# Revit family: Capsule V 2100-12500
name_source: partatom
category: Оборудование
units: mm (PartAtom-declared; Revit-internal decimal feet)

## family parameters
Всегда вертикально = Да
Классификация = Нет
На основе рабочей плоскости = Нет
Общий = Нет
При загрузке вырезать с полостями = Нет
Размер круглого соединителя = Использовать диаметр
Тип детали = Нормальный
Точка расчета площади = Нет

## types (10) — shared parameters
ADSK_Единица измерения = шт.
ADSK_Завод-изготовитель = ООО «Турков»
ADSK_Количество = 1
ADSK_Наименование = Вытяжная установка
КА длина = 180 мм
КА ширина = 82 мм
Крепеж Y = 23 мм
Толщина крышки = 50 мм
высота КА = 52 мм

## per-type parameters (varying)
| type | A ширина | ADSK_Количество фаз | ADSK_Масса | ADSK_Напряжение | ADSK_Номинальная мощность | ADSK_Расход воздуха приточный | ADSK_Свободный напор воздуха | ADSK_Ток | B высота | ВВ длина | ВВ толщина | ВВ ширина | Крепеж X | С глубина | СЗ_фильтры |
| VBox 6100 | 635 мм | 1 | 75 | 220 В | 330 Вт | 600.0 м³/ч | 189.0 Па | 1 А | 900 мм | 800 мм | 180 мм | 500 мм | 52 мм | 650 мм | 350 мм |
| VBox 4100 | 635 мм | 1 | 100 | 220 В | 840 Вт | 4000.0 м³/ч | 253.0 Па | 2 А | 850 мм | 700 мм | 190 мм | 400 мм | 7 мм | 550 мм | 400 мм |
| VBox 2100 | 528 мм | 1 | 75 | 220 В | 330 Вт | 2100.0 м³/ч | 189.0 Па | 1 А | 656 мм | 500 мм | 180 мм | 250 мм | 52 мм | 437 мм | 350 мм |
| VBox 3100 | 635 мм | 1 | 80 | 220 В | 750 Вт | 3000.0 м³/ч | 291.0 Па | 5 А | 750 мм | 600 мм | 190 мм | 300 мм | 52 мм | 450 мм | 300 мм |
| VBox 5100 | 635 мм | 3 | 105 | 380 В | 2500 Вт | 5000.0 м³/ч | 620.0 Па | 4 А | 850 мм | 700 мм | 190 мм | 400 мм | 7 мм | 550 мм | 400 мм |
| VBox 7100 | 635 мм | 3 | 120 | 380 В | 0 Вт | 6000.0 м³/ч | 291.0 Па | 0 А | 900 мм | 800 мм | 190 мм | 500 мм | 52 мм | 650 мм | 500 мм |
| VBox 8100 | 735 мм | 3 | 120 | 380 В | 3800 Вт | 8000.0 м³/ч | 1009.0 Па | 6 А | 1000 мм | 900 мм | 190 мм | 500 мм | 52 мм | 650 мм | 500 мм |
| VBox 9100 | 735 мм | 3 | 155 | 380 В | 3800 Вт | 9000.0 м³/ч | 750.0 Па | 6 А | 1100 мм | 1000 мм | 190 мм | 500 мм | 52 мм | 650 мм | 500 мм |
| VBox 10100 | 835 мм | 3 | 180 | 380 В | 4500 Вт | 10000.0 м³/ч | 959.0 Па | 7 А | 1100 мм | 1000 мм | 190 мм | 800 мм | 52 мм | 950 мм | 500 мм |
| VBox 12600 | 835 мм | 3 | 185 | 380 В | 5700 Вт | 12500.0 м³/ч | 645.0 Па | 9 А | 1100 мм | 1000 мм | 190 мм | 800 мм | 52 мм | 950 мм | 500 мм |

note: column(s) folded — value = type name in every type: ADSK_Марка
